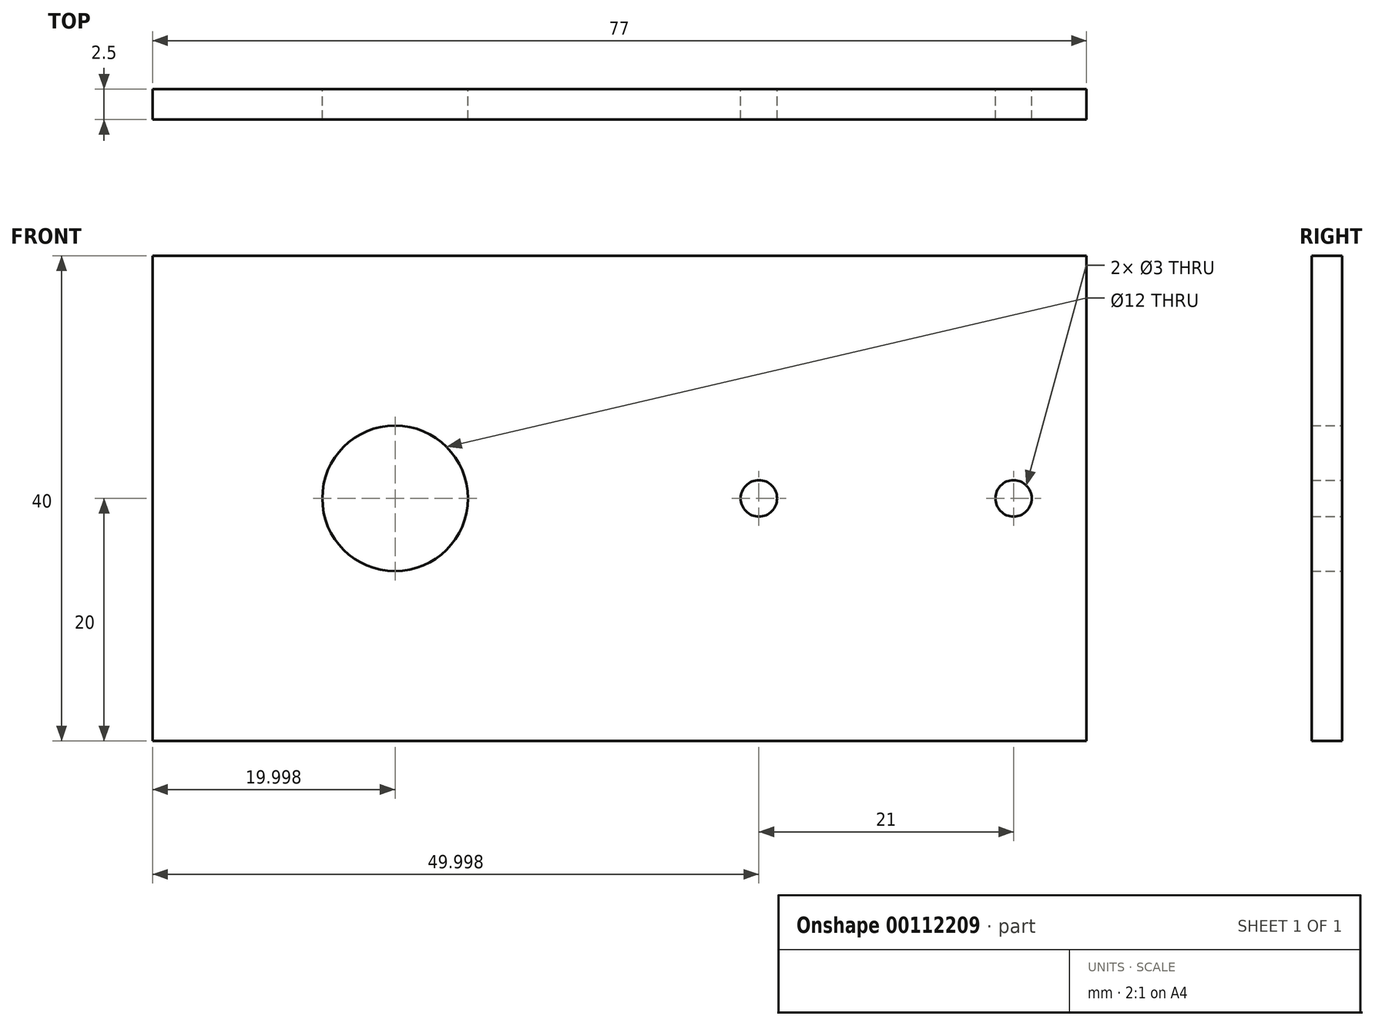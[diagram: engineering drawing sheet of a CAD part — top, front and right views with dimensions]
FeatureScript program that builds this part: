
annotation { "Feature Type Name" : "Feature", "Feature Type Description" : "" }
export const myFeature = defineFeature(function(context is Context, id is Id, definition is map)
    precondition{}
    {
        {
            var Q0;
            Q0=qCreatedBy(makeId("Front.planeOp"),FACE);
            var sketch = newSketch(context, id + "F0", { "sketchPlane" : qUnion([Q0])});
            skLineSegment(sketch, "E0.bottom", {"start": v(-79.41, 0) * mm, "end": v(-2.41, 0) * mm});
            skLineSegment(sketch, "E0.top", {"start": v(-79.41, 40) * mm, "end": v(-2.41, 40) * mm});
            skLineSegment(sketch, "E0.left", {"start": v(-79.41, 0) * mm, "end": v(-79.41, 40) * mm});
            skLineSegment(sketch, "E0.right", {"start": v(-2.41, 0) * mm, "end": v(-2.41, 40) * mm});
            skCircle(sketch, "E1", {"center": v(-59.41, 20) * mm, "radius": 6 * mm});
            skPoint(sketch, "E1.centerSnap0", {"position": v(-79.41, 20) * mm});
            skCircle(sketch, "E2", {"center": v(-29.41, 20) * mm, "radius": 1.5 * mm});
            skCircle(sketch, "E3", {"center": v(-8.41, 20) * mm, "radius": 1.5 * mm});
            skSolve(sketch);
        }
        {
            var Q0;
            Q0=makeQuery(id+"F0.imprint","IMPRINT",FACE,{"disambiguationData":[TD([[makeQuery(id+"F0.imprint","IMPRINT",EDGE,{"derivedFrom":sQuery(id+"F0.wireOp",EDGE,"E0.bottom")}),1.0]])]});
            extrude(context, id + "F1", {"entities" : qUnion([Q0]), "depth" : 2.5 * mm});
        }
    });
